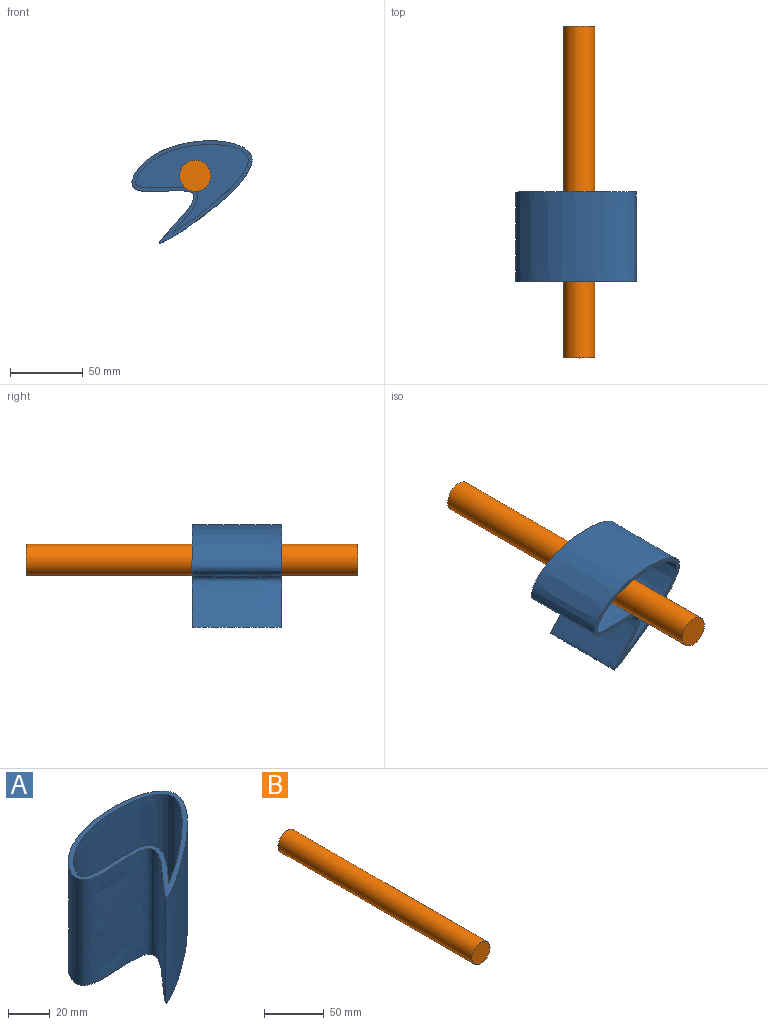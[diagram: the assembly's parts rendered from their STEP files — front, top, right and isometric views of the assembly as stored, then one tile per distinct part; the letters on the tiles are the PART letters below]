
ASSEMBLY  parts=2 mates=1
PART A: 6 faces, bbox 88.6x78.1x61.7 mm
  f0: extruded ~82.57x70.53mm, area 17019.1mm2, adj f1,f2
  f1: plane 88.57x78.14mm, normal (0,0,1), area 668.7mm2, adj f0,f3,f4
  f2: plane 88.57x78.14mm, normal (0,0,-1), area 2821.7mm2, adj f0
  f3: extruded ~59.18x51.92mm, area 6058.1mm2, adj f1,f4,f5
  f4: extruded ~62.91x61.04mm, area 8455.3mm2, adj f1,f3,f5
  f5: plane 77.64x61.06mm, normal (0,0,1), area 2152.6mm2, adj f3,f4
PART B: 3 faces, bbox 21.5x228.6x21.5 mm
  f0: cylinder r=10.73mm len=228.6mm, axis (0,-1,0), area 15409.5mm2, adj f1,f2
  f1: plane 21.46x21.46mm, normal (0,1,0), area 361.6mm2, adj f0
  f2: plane 21.46x21.46mm, normal (0,-1,0), area 361.6mm2, adj f0
PLACE A rot(axis=(1,0,0),90deg) t=(26.51,-0.6,-71.28)mm
PLACE B t=(-124.23,12.1,-65.4)mm
MATE pin_slot A.f2 <-> B.f0  axis (0,1,0) through (-102.34,-0.6,-3.62)mm
